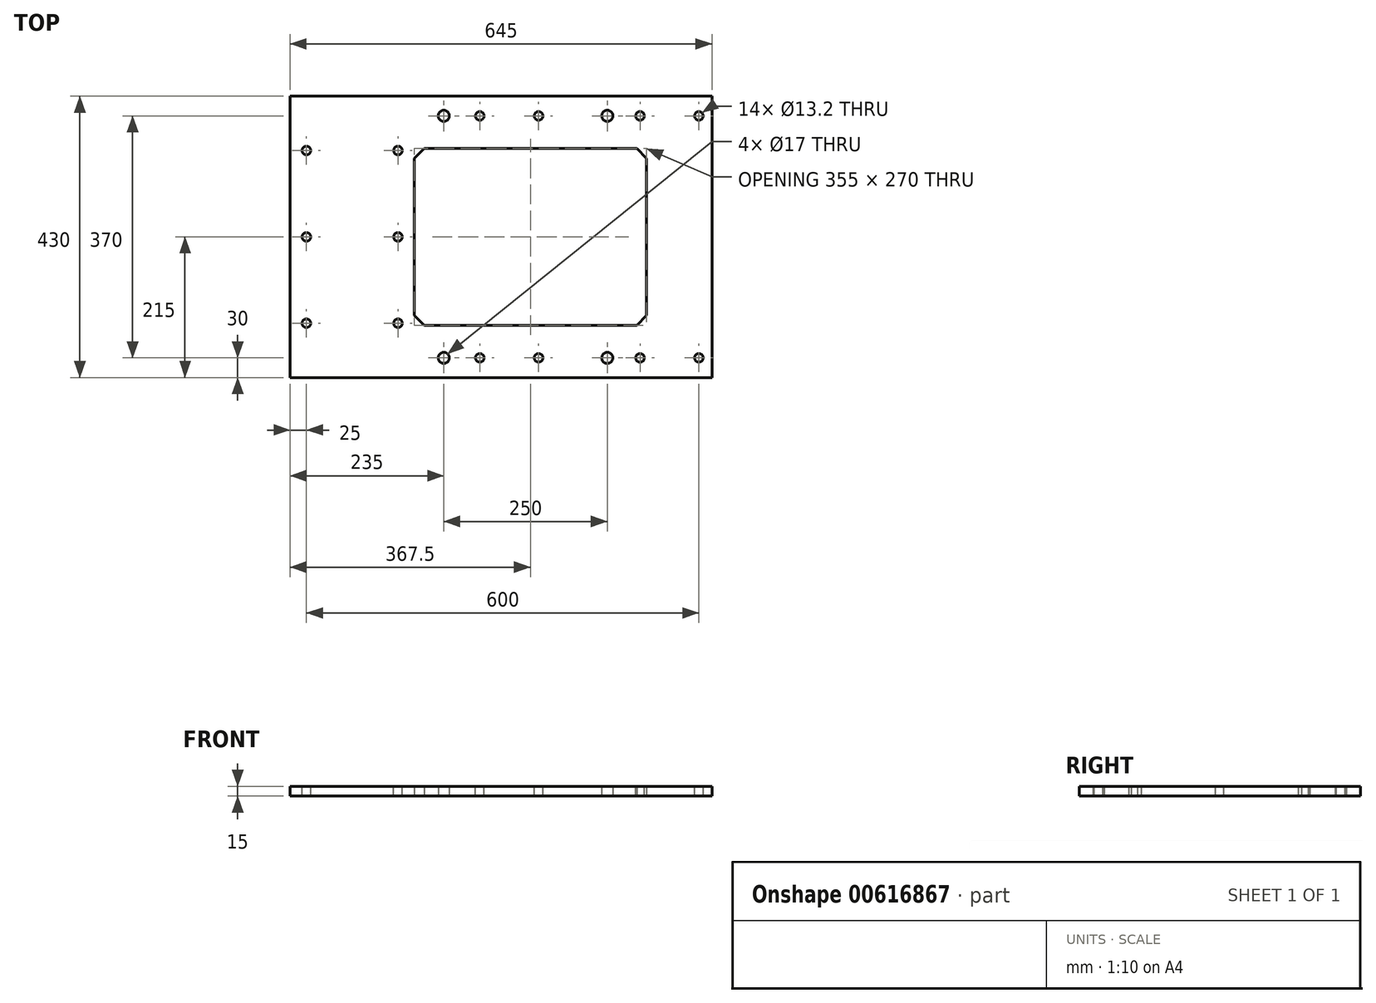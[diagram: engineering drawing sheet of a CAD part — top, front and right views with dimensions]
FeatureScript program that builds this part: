
annotation { "Feature Type Name" : "Feature", "Feature Type Description" : "" }
export const myFeature = defineFeature(function(context is Context, id is Id, definition is map)
    precondition{}
    {
        {
            var Q0;
            Q0=qCreatedBy(makeId("Top.planeOp"),FACE);
            var sketch = newSketch(context, id + "F0", { "sketchPlane" : qUnion([Q0])});
            skLineSegment(sketch, "E0.bottom", {"start": v(322.5, 215) * mm, "end": v(-322.5, 215) * mm});
            skLineSegment(sketch, "E0.top", {"start": v(322.5, -215) * mm, "end": v(-322.5, -215) * mm});
            skLineSegment(sketch, "E0.left", {"start": v(322.5, 215) * mm, "end": v(322.5, -215) * mm});
            skLineSegment(sketch, "E0.right", {"start": v(-322.5, 215) * mm, "end": v(-322.5, -215) * mm});
            skPoint(sketch, "E0.middle", {"position": v(0, 0) * mm});
            skLineSegment(sketch, "E1.bottom", {"start": v(-117.5, 135) * mm, "end": v(207.5, 135) * mm});
            skLineSegment(sketch, "E1.top", {"start": v(-117.5, -135) * mm, "end": v(207.5, -135) * mm});
            skLineSegment(sketch, "E1.left", {"start": v(-132.5, 120) * mm, "end": v(-132.5, -120) * mm});
            skLineSegment(sketch, "E1.right", {"start": v(222.5, 120) * mm, "end": v(222.5, -120) * mm});
            skLineSegment(sketch, "E2", {"start": v(-132.5, 120) * mm, "end": v(-117.5, 135) * mm});
            skLineSegment(sketch, "E3", {"start": v(207.5, 135) * mm, "end": v(222.5, 120) * mm});
            skLineSegment(sketch, "E4", {"start": v(-132.5, -120) * mm, "end": v(-117.5, -135) * mm});
            skLineSegment(sketch, "E5", {"start": v(207.5, -135) * mm, "end": v(222.5, -120) * mm});
            skSolve(sketch);
        }
        {
            var Q0;
            Q0 = qSketchRegion(id + "F0", true);
            extrude(context, id + "F1", {"entities" : qUnion([Q0]), "depth" : 15 * mm, "offsetDistance" : 25 * mm});
        }
        {
            var Q0;
            Q0=qCreatedBy(makeId("Top.planeOp"),FACE);
            var sketch = newSketch(context, id + "F2", { "sketchPlane" : qUnion([Q0])});
            skLineSegment(sketch, "E6.0", {"start": v(322.5, 215) * mm, "end": v(-322.5, 215) * mm, "construction": true});
            skLineSegment(sketch, "E7.0", {"start": v(322.5, 215) * mm, "end": v(322.5, -215) * mm, "construction": true});
            skLineSegment(sketch, "E8.0", {"start": v(322.5, -215) * mm, "end": v(-322.5, -215) * mm, "construction": true});
            skLineSegment(sketch, "E9.0", {"start": v(-322.5, 215) * mm, "end": v(-322.5, -215) * mm, "construction": true});
            skLineSegment(sketch, "E10", {"start": v(-297.5, 215) * mm, "end": v(-297.5, -215) * mm, "construction": true});
            skLineSegment(sketch, "E11", {"start": v(-157.5, 215) * mm, "end": v(-157.5, -215) * mm, "construction": true});
            skLineSegment(sketch, "E12", {"start": v(-32.5, 215) * mm, "end": v(-32.5, -215) * mm, "construction": true});
            skLineSegment(sketch, "E13", {"start": v(57.5, 215) * mm, "end": v(57.5, -215) * mm, "construction": true});
            skLineSegment(sketch, "E14", {"start": v(212.5, 215) * mm, "end": v(212.5, -215) * mm, "construction": true});
            skLineSegment(sketch, "E15", {"start": v(302.5, 215) * mm, "end": v(302.5, -215) * mm, "construction": true});
            skLineSegment(sketch, "E16", {"start": v(322.5, 185) * mm, "end": v(-322.5, 185) * mm, "construction": true});
            skLineSegment(sketch, "E17", {"start": v(322.5, -185) * mm, "end": v(-322.5, -185) * mm, "construction": true});
            skPoint(sketch, "E18", {"position": v(302.5, 185) * mm});
            skPoint(sketch, "E19", {"position": v(212.5, 185) * mm});
            skPoint(sketch, "E20", {"position": v(57.5, 185) * mm});
            skPoint(sketch, "E21", {"position": v(-32.5, 185) * mm});
            skPoint(sketch, "E22", {"position": v(-32.5, -185) * mm});
            skPoint(sketch, "E23", {"position": v(57.5, -185) * mm});
            skPoint(sketch, "E24", {"position": v(302.5, -185) * mm});
            skPoint(sketch, "E25", {"position": v(212.5, -185) * mm});
            skLineSegment(sketch, "E26", {"start": v(-322.5, 132) * mm, "end": v(-157.5, 132) * mm, "construction": true});
            skLineSegment(sketch, "E27", {"start": v(-322.5, 0) * mm, "end": v(-157.5, 0) * mm, "construction": true});
            skLineSegment(sketch, "E28", {"start": v(-322.5, -132) * mm, "end": v(-157.5, -132) * mm, "construction": true});
            skPoint(sketch, "E29", {"position": v(-157.5, 132) * mm});
            skPoint(sketch, "E30", {"position": v(-297.5, 132) * mm});
            skPoint(sketch, "E31", {"position": v(-157.5, 0) * mm});
            skPoint(sketch, "E32", {"position": v(-297.5, 0) * mm});
            skPoint(sketch, "E33", {"position": v(-297.5, -132) * mm});
            skPoint(sketch, "E34", {"position": v(-157.5, -132) * mm});
            skSolve(sketch);
        }
        {
            var Q0;
            Q0=sQuery(id+"F2.wireOp",VERTEX,"E30");
            var Q1;
            Q1=sQuery(id+"F2.wireOp",VERTEX,"E32");
            var Q2;
            Q2=sQuery(id+"F2.wireOp",VERTEX,"E33");
            var Q3;
            Q3=sQuery(id+"F2.wireOp",VERTEX,"E29");
            var Q4;
            Q4=sQuery(id+"F2.wireOp",VERTEX,"E31");
            var Q5;
            Q5=sQuery(id+"F2.wireOp",VERTEX,"E34");
            var Q6;
            Q6=sQuery(id+"F2.wireOp",VERTEX,"E22");
            var Q7;
            Q7=sQuery(id+"F2.wireOp",VERTEX,"E23");
            var Q8;
            Q8=sQuery(id+"F2.wireOp",VERTEX,"E25");
            var Q9;
            Q9=sQuery(id+"F2.wireOp",VERTEX,"E24");
            var Q10;
            Q10=sQuery(id+"F2.wireOp",VERTEX,"E18");
            var Q11;
            Q11=sQuery(id+"F2.wireOp",VERTEX,"E19");
            var Q12;
            Q12=sQuery(id+"F2.wireOp",VERTEX,"E20");
            var Q13;
            Q13=sQuery(id+"F2.wireOp",VERTEX,"E21");
            var Q14;
            Q14=makeQuery(id+"F1.opExtrude","SWEPT_BODY",BODY,{"disambiguationData":[OSD([sQuery(id+"F0.wireOp",EDGE,"E0.bottom"),sQuery(id+"F0.wireOp",EDGE,"E0.top"),sQuery(id+"F0.wireOp",EDGE,"E0.left"),sQuery(id+"F0.wireOp",EDGE,"E0.right"),sQuery(id+"F0.wireOp",EDGE,"E1.bottom"),sQuery(id+"F0.wireOp",EDGE,"E1.top"),sQuery(id+"F0.wireOp",EDGE,"E1.left"),sQuery(id+"F0.wireOp",EDGE,"E1.right"),sQuery(id+"F0.wireOp",EDGE,"E2"),sQuery(id+"F0.wireOp",EDGE,"E3"),sQuery(id+"F0.wireOp",EDGE,"E4"),sQuery(id+"F0.wireOp",EDGE,"E5")])]});
            hole(context, id + "F3", {"style" : HoleStyle.SIMPLE, "endStyle" : HoleEndStyle.THROUGH, "oppositeDirection" : true, "standardTappedOrClearance" : lookupTablePath({ "standard" : "ISO", "fit" : "Normal", "size" : "M12", "type" : "Clearance" }), "standardBlindInLast" : lookupTablePath({ "fit" : "Standard", "standard" : "ISO", "size" : "M12", "type" : "Clearance" }), "holeDiameter" : 13.2 * mm, "majorDiameter" : 5 * mm, "isTappedThrough" : true, "tappedDepth" : 12 * mm, "tapClearance" : 3, "locations" : qUnion([Q0, Q1, Q2, Q3, Q4, Q5, Q6, Q7, Q8, Q9, Q10, Q11, Q12, Q13]), "scope" : qUnion([Q14]), "startStyle" : HoleStartStyle.PART});
        }
        {
            var Q0;
            Q0=qCreatedBy(makeId("Top.planeOp"),FACE);
            var sketch = newSketch(context, id + "F4", { "sketchPlane" : qUnion([Q0])});
            skLineSegment(sketch, "E35.0", {"start": v(322.5, 215) * mm, "end": v(-322.5, 215) * mm, "construction": true});
            skLineSegment(sketch, "E36.0", {"start": v(322.5, 215) * mm, "end": v(322.5, -215) * mm, "construction": true});
            skLineSegment(sketch, "E37.0", {"start": v(322.5, -215) * mm, "end": v(-322.5, -215) * mm, "construction": true});
            skLineSegment(sketch, "E38.0", {"start": v(-322.5, 215) * mm, "end": v(-322.5, -215) * mm, "construction": true});
            skLineSegment(sketch, "E39", {"start": v(322.5, -185) * mm, "end": v(-322.5, -185) * mm, "construction": true});
            skLineSegment(sketch, "E40", {"start": v(322.5, 185) * mm, "end": v(-322.5, 185) * mm, "construction": true});
            skLineSegment(sketch, "E41", {"start": v(162.5, 215) * mm, "end": v(162.5, -215) * mm, "construction": true});
            skLineSegment(sketch, "E42", {"start": v(-87.5, 215) * mm, "end": v(-87.5, -215) * mm, "construction": true});
            skCircle(sketch, "E43", {"center": v(-87.5, 185) * mm, "radius": 8.5 * mm});
            skCircle(sketch, "E44", {"center": v(162.5, 185) * mm, "radius": 8.5 * mm});
            skCircle(sketch, "E45", {"center": v(162.5, -185) * mm, "radius": 8.5 * mm});
            skCircle(sketch, "E46", {"center": v(-87.5, -185) * mm, "radius": 8.5 * mm});
            skSolve(sketch);
        }
        {
            var Q0;
            Q0 = qSketchRegion(id + "F4", true);
            extrude(context, id + "F5", {"entities" : qUnion([Q0]), "operationType" : NewBodyOperationType.REMOVE, "endBound" : BoundingType.UP_TO_NEXT, "depth" : 25 * mm, "offsetDistance" : 25 * mm});
        }
    });
